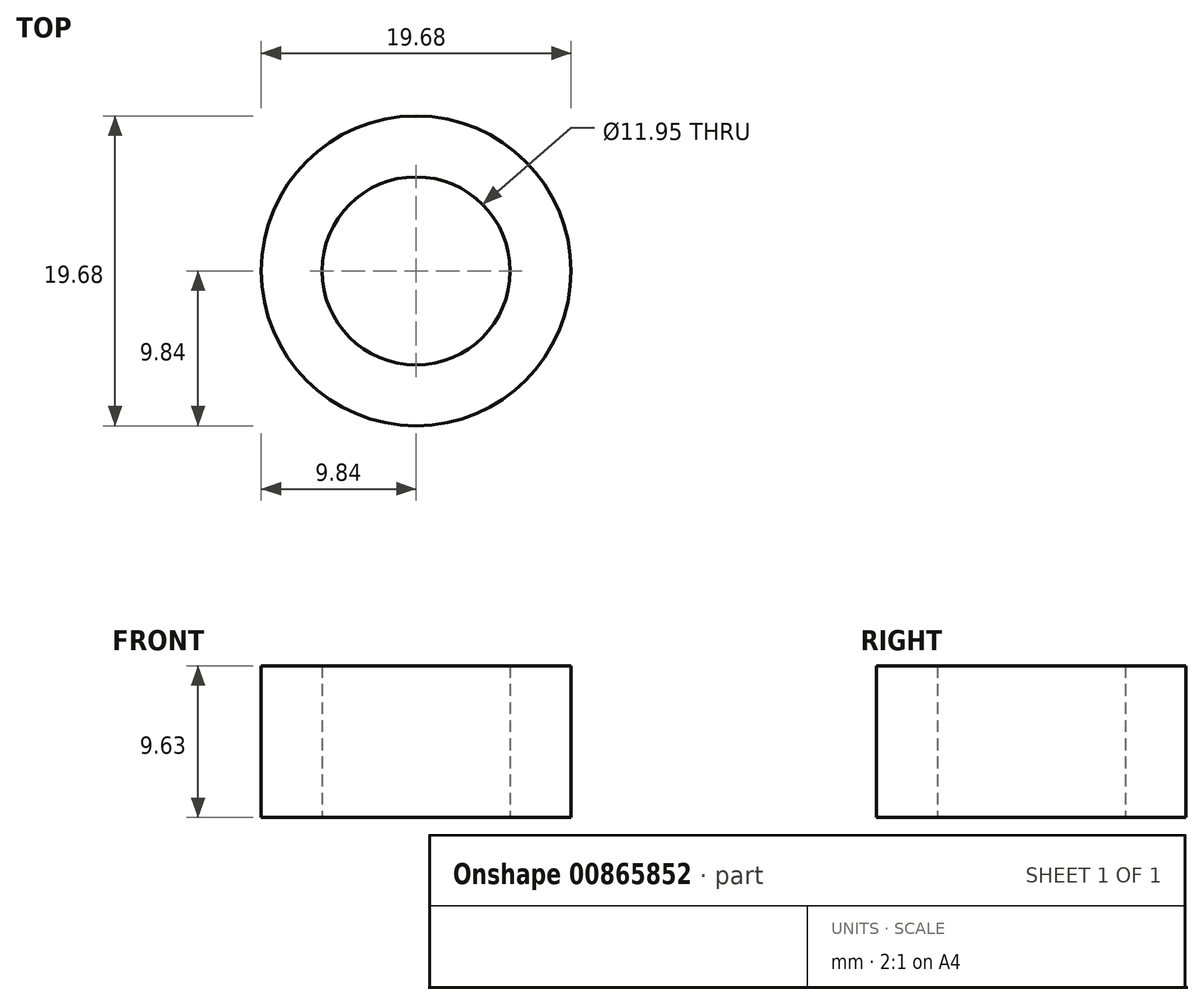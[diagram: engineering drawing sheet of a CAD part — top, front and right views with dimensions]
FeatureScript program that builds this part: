
annotation { "Feature Type Name" : "Feature", "Feature Type Description" : "" }
export const myFeature = defineFeature(function(context is Context, id is Id, definition is map)
    precondition{}
    {
        {
            var Q0;
            Q0=qCreatedBy(makeId("Top.planeOp"),FACE);
            var sketch = newSketch(context, id + "F0", { "sketchPlane" : qUnion([Q0])});
            skCircle(sketch, "E0", {"center": v(0, 0) * mm, "radius": 9.84 * mm});
            skCircle(sketch, "E1", {"center": v(0, 0) * mm, "radius": 5.97 * mm});
            skSolve(sketch);
        }
        {
            var Q0;
            Q0 = qSketchRegion(id + "F0", true);
            extrude(context, id + "F1", {"entities" : qUnion([Q0]), "depth" : 9.63 * mm, "offsetDistance" : 25.4 * mm});
        }
    });
